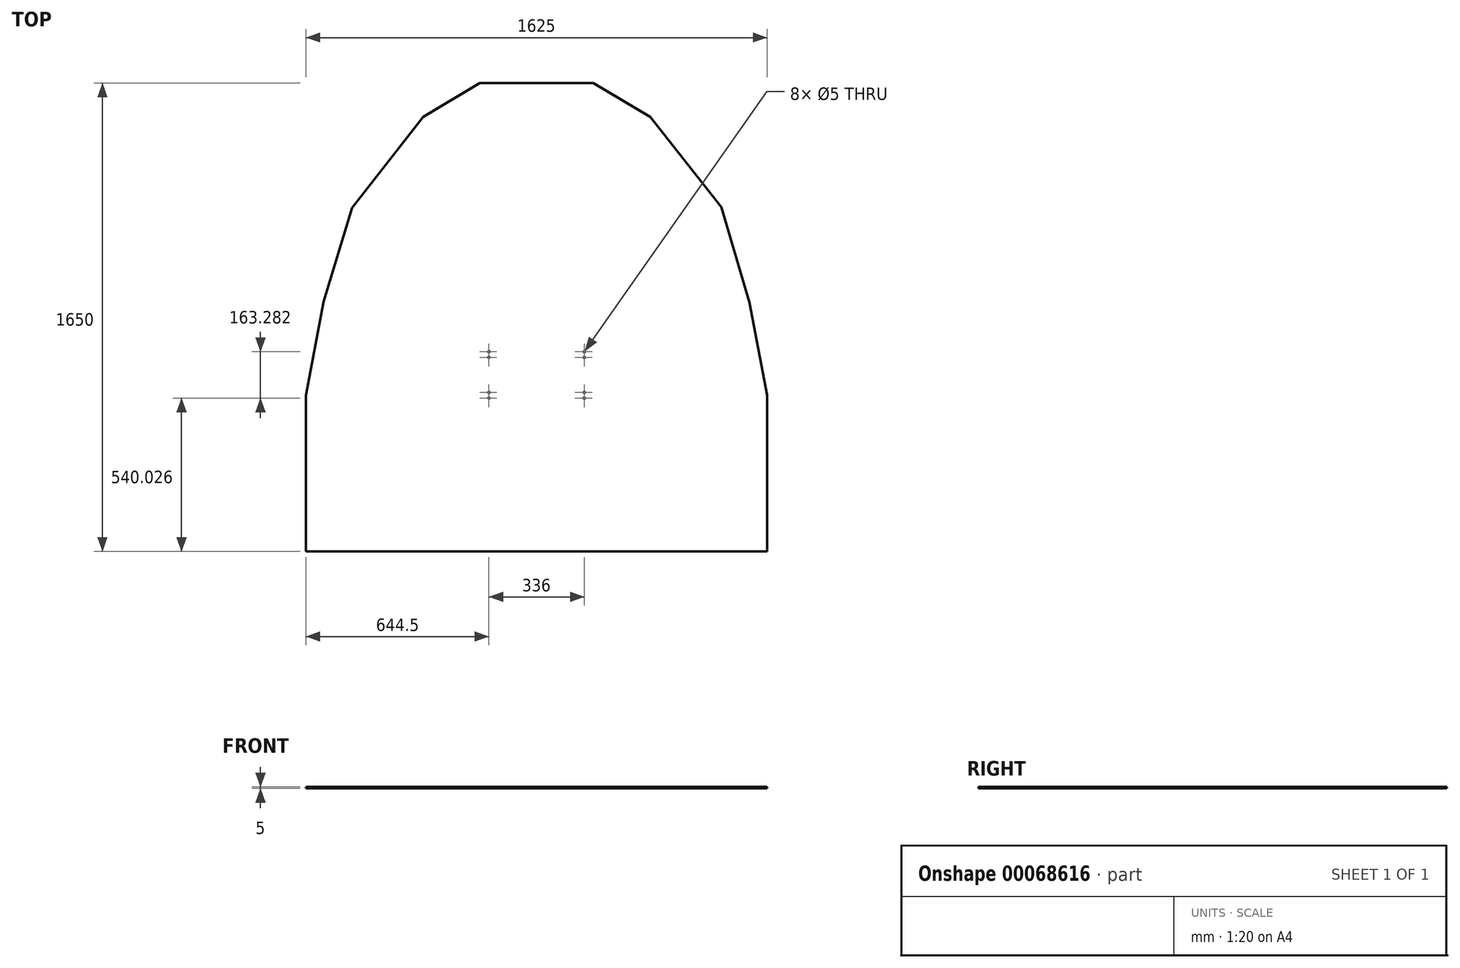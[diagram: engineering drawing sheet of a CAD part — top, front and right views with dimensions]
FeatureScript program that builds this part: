
annotation { "Feature Type Name" : "Feature", "Feature Type Description" : "" }
export const myFeature = defineFeature(function(context is Context, id is Id, definition is map)
    precondition{}
    {
        {
            var Q0;
            Q0=qCreatedBy(makeId("Top.planeOp"),FACE);
            var sketch = newSketch(context, id + "F0", { "sketchPlane" : qUnion([Q0])});
            skLineSegment(sketch, "E0.bottom", {"start": v(-812.5, -277.75) * mm, "end": v(812.5, -277.75) * mm});
            skLineSegment(sketch, "E0.top", {"start": v(-812.5, -827.75) * mm, "end": v(812.5, -827.75) * mm});
            skLineSegment(sketch, "E0.left", {"start": v(-812.5, -277.75) * mm, "end": v(-812.5, -827.75) * mm});
            skLineSegment(sketch, "E0.right", {"start": v(812.5, -277.75) * mm, "end": v(812.5, -827.75) * mm});
            skLineSegment(sketch, "E1", {"start": v(-812.5, -277.75) * mm, "end": v(-750, 52.25) * mm});
            skLineSegment(sketch, "E2", {"start": v(-750, 52.25) * mm, "end": v(750, 47.94) * mm});
            skLineSegment(sketch, "E3", {"start": v(750, 47.94) * mm, "end": v(812.5, -277.75) * mm});
            skLineSegment(sketch, "E4", {"start": v(-750, 52.25) * mm, "end": v(-650, 382.25) * mm});
            skLineSegment(sketch, "E5", {"start": v(-650, 382.25) * mm, "end": v(650, 384.5) * mm});
            skLineSegment(sketch, "E6", {"start": v(650, 384.5) * mm, "end": v(750, 47.94) * mm});
            skLineSegment(sketch, "E7", {"start": v(-650, 382.25) * mm, "end": v(-400, 702.25) * mm});
            skLineSegment(sketch, "E8", {"start": v(-400, 702.25) * mm, "end": v(400, 702.25) * mm});
            skLineSegment(sketch, "E9", {"start": v(400, 702.25) * mm, "end": v(650, 384.5) * mm});
            skLineSegment(sketch, "E10", {"start": v(0, 218.8) * mm, "end": v(0, -2047.11) * mm, "construction": true});
            skLineSegment(sketch, "E11", {"start": v(-400, 702.25) * mm, "end": v(-200, 822.25) * mm});
            skLineSegment(sketch, "E12", {"start": v(-200, 822.25) * mm, "end": v(200, 822.2) * mm});
            skLineSegment(sketch, "E13", {"start": v(200, 822.2) * mm, "end": v(400, 702.25) * mm});
            skCircle(sketch, "E14", {"center": v(168, -144.44) * mm, "radius": 2.5 * mm});
            skCircle(sketch, "E15", {"center": v(168, -124.44) * mm, "radius": 2.5 * mm});
            skCircle(sketch, "E16", {"center": v(168, -267.72) * mm, "radius": 2.5 * mm});
            skCircle(sketch, "E17", {"center": v(168, -287.72) * mm, "radius": 2.5 * mm});
            skCircle(sketch, "E18.MirrorC", {"center": v(-168, -287.72) * mm, "radius": 2.5 * mm});
            skCircle(sketch, "E19.MirrorC", {"center": v(-168, -267.72) * mm, "radius": 2.5 * mm});
            skCircle(sketch, "E20.MirrorC", {"center": v(-168, -144.44) * mm, "radius": 2.5 * mm});
            skCircle(sketch, "E21.MirrorC", {"center": v(-168, -124.44) * mm, "radius": 2.5 * mm});
            skSolve(sketch);
        }
        {
            var Q0;
            Q0 = qSketchRegion(id + "F0", true);
            extrude(context, id + "F1", {"entities" : qUnion([Q0]), "oppositeDirection" : true, "depth" : 5 * mm});
        }
    });
